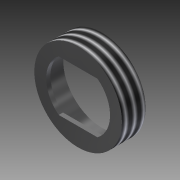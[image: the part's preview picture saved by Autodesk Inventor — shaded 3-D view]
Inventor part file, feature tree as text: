
AUTODESK INVENTOR PART (.ipt)
format: ipt  version: 2012 (Build 160160000, 160)  size: 100,352 bytes
history: native  units: in
note: dims shown in document units (in); Inventor stores cm internally (conversion verified against a paired STEP export)
features: extrude x2, sketch x1, thread x1
ambient origin geometry x8: Origin, YZ Plane, XZ Plane, XY Plane, X Axis, Y Axis, Z Axis, Center Point
bodies: Solid1 (feature_tree)
feature tree (4):
  sketch  "Sketch1"  dims[d0=1.645in d1=1.2in d2=0.4765in d3=0.4765in d4=1.452in d5=0.366in d6=0.0in d7=0.08in d8=0.0in d9=1.0in d10=0.0in]
  extrude  "Extrusion1"  Depth=1.2in
  extrude  "Extrusion2"  Depth=0.4765in
  thread  "Thread1"  [1 undecoded]
note: 1 required parameter value undecoded (feature->parameter linkage not recoverable at this tier; creation-order binding heuristic only, values carry confidence <= 0.55)
